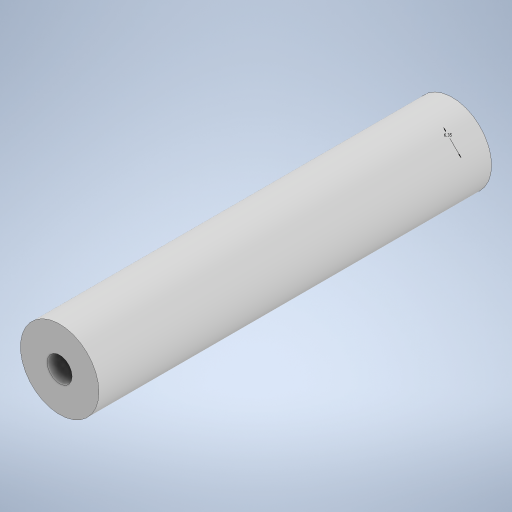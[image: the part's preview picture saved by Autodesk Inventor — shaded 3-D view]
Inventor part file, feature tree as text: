
AUTODESK INVENTOR PART (.ipt)
format: ipt  version: 2024 (Build 280153000, 153)  size: 225,792 bytes
history: native  units: in
note: dims shown in document units (in); Inventor stores cm internally (conversion verified against a paired STEP export)
features: sketch x3, extrude x2
ambient origin geometry x8: Origin, YZ Plane, XZ Plane, XY Plane, X Axis, Y Axis, Z Axis, Center Point
bodies: Solid1 (feature_tree)
feature tree (5):
  extrude  "Extrusion1"  Depth=3.937in TaperAngle=0.0deg
  extrude  "Extrusion2"  Depth=0.7874in TaperAngle=0.0deg
  sketch  "Sketch3"  dims[d6=0.25in]
  sketch  "Sketch1"  dims[d0=0.7874in d1=3.937in d2=0.0in]
  sketch  "Sketch2"  dims[d3=0.25in d4=0.7874in d5=0.0in]
